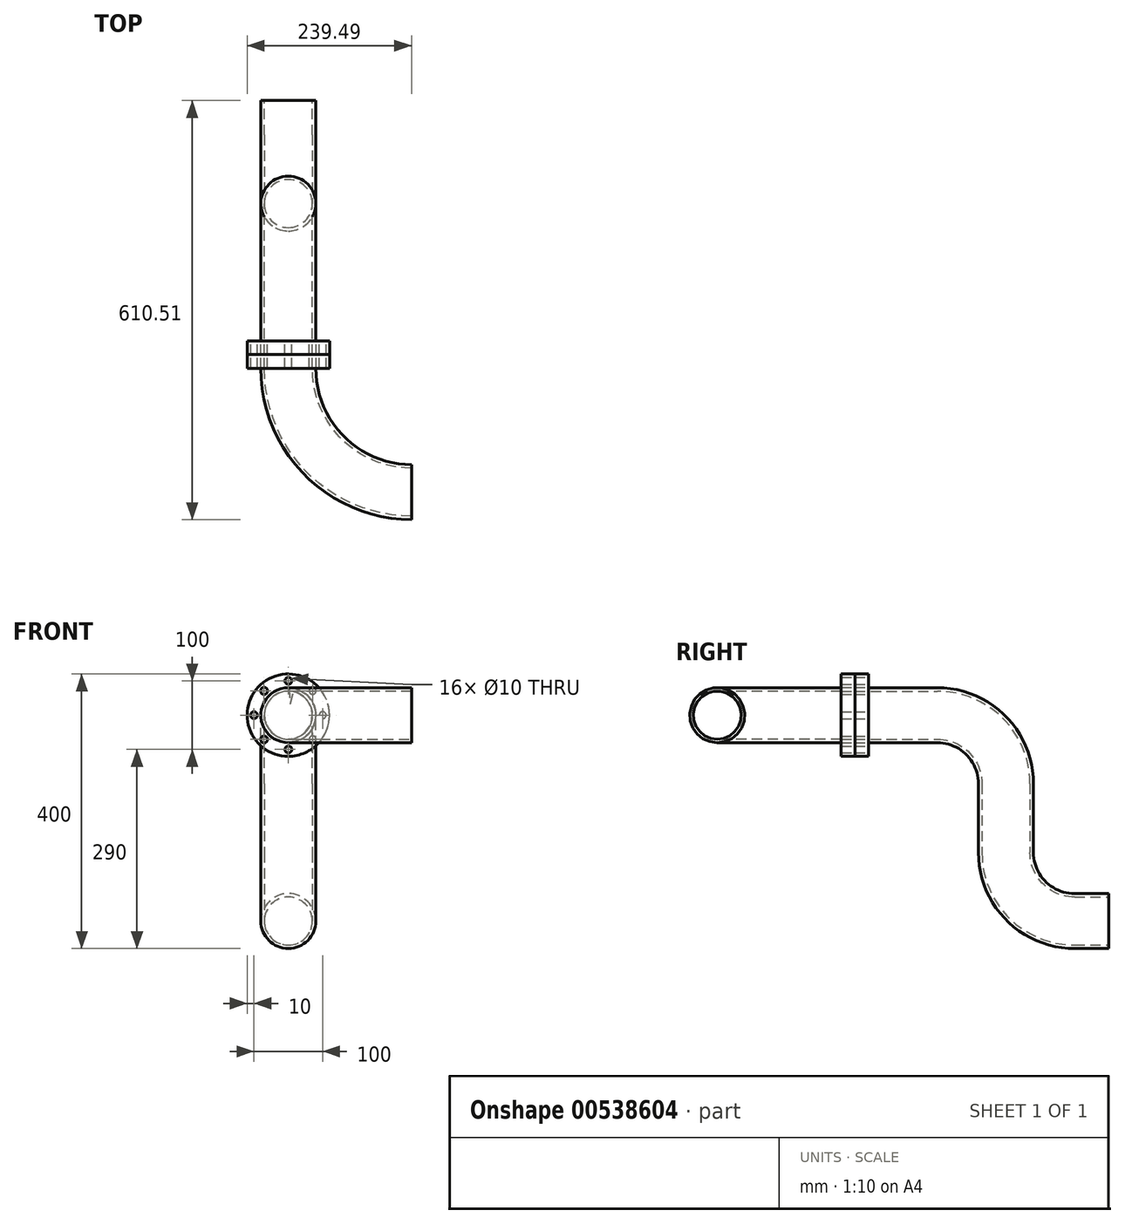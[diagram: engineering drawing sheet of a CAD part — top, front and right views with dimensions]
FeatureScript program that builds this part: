
annotation { "Feature Type Name" : "Feature", "Feature Type Description" : "" }
export const myFeature = defineFeature(function(context is Context, id is Id, definition is map)
    precondition{}
    {
        {
            var Q0;
            Q0=qCreatedBy(makeId("Front.planeOp"),FACE);
            var sketch = newSketch(context, id + "F0", { "sketchPlane" : qUnion([Q0])});
            skCircle(sketch, "E0", {"center": v(0, 0) * mm, "radius": 60 * mm});
            skCircle(sketch, "E1", {"center": v(0, 50) * mm, "radius": 5 * mm});
            skCircle(sketch, "E2.1.0", {"center": v(-35.36, 35.36) * mm, "radius": 5 * mm});
            skCircle(sketch, "E2.2.0", {"center": v(-50, 0) * mm, "radius": 5 * mm});
            skCircle(sketch, "E2.3.0", {"center": v(-35.36, -35.36) * mm, "radius": 5 * mm});
            skCircle(sketch, "E2.4.0", {"center": v(0, -50) * mm, "radius": 5 * mm});
            skCircle(sketch, "E2.5.0", {"center": v(35.36, -35.36) * mm, "radius": 5 * mm});
            skCircle(sketch, "E2.6.0", {"center": v(50, 0) * mm, "radius": 5 * mm});
            skCircle(sketch, "E2.7.0", {"center": v(35.36, 35.36) * mm, "radius": 5 * mm});
            skCircle(sketch, "E3", {"center": v(0, 0) * mm, "radius": 35 * mm});
            skSolve(sketch);
        }
        {
            var Q0;
            Q0 = qSketchRegion(id + "F0", true);
            extrude(context, id + "F1", {"entities" : qUnion([Q0]), "depth" : 20 * mm, "offsetDistance" : 25 * mm});
        }
        {
            var Q0;
            Q0=qCreatedBy(makeId("Front.planeOp"),FACE);
            var sketch = newSketch(context, id + "F2", { "sketchPlane" : qUnion([Q0])});
            skCircle(sketch, "E4", {"center": v(0, 0) * mm, "radius": 40 * mm});
            skCircle(sketch, "E5", {"center": v(0, 0) * mm, "radius": 35 * mm});
            skSolve(sketch);
        }
        {
            var Q0;
            Q0=qCreatedBy(makeId("Right.planeOp"),FACE);
            var sketch = newSketch(context, id + "F3", { "sketchPlane" : qUnion([Q0])});
            skLineSegment(sketch, "E6", {"start": v(0, 0) * mm, "end": v(100, 0) * mm});
            skLineSegment(sketch, "E7", {"start": v(200, -100) * mm, "end": v(200, -200) * mm});
            skLineSegment(sketch, "E8", {"start": v(300, -300) * mm, "end": v(350, -300) * mm});
            skPoint(sketch, "E9.visualSharp", {"position": v(200, 0) * mm});
            skArc(sketch, "E9.filletArc", {"start": v(200, -100) * mm, "mid": v(170.71, -29.29) * mm, "end": v(100, 0) * mm});
            skPoint(sketch, "E10.visualSharp", {"position": v(200, -300) * mm});
            skArc(sketch, "E10.filletArc", {"start": v(200, -200) * mm, "mid": v(229.29, -270.71) * mm, "end": v(300, -300) * mm});
            skSolve(sketch);
        }
        {
            var Q0;
            Q0=makeQuery(id+"F2.imprint","IMPRINT",FACE,{"disambiguationData":[TD([[makeQuery(id+"F2.imprint","IMPRINT",EDGE,{"derivedFrom":sQuery(id+"F2.wireOp",EDGE,"E4")}),1.0]])]});
            var Q1;
            Q1=sQuery(id+"F3.wireOp",EDGE,"E6");
            var Q2;
            Q2=sQuery(id+"F3.wireOp",EDGE,"E9.filletArc");
            var Q3;
            Q3=sQuery(id+"F3.wireOp",EDGE,"E7");
            var Q4;
            Q4=sQuery(id+"F3.wireOp",EDGE,"E10.filletArc");
            var Q5;
            Q5=sQuery(id+"F3.wireOp",EDGE,"E8");
            sweep(context, id + "F4", {"operationType" : NewBodyOperationType.ADD, "profiles" : qUnion([Q0]), "path" : qUnion([Q1, Q2, Q3, Q4, Q5])});
        }
        {
            var Q0;
            Q0=makeQuery(id+"F1.opExtrude","CAP_FACE",FACE,{"disambiguationData":[OSD([sQuery(id+"F0.wireOp",EDGE,"E0"),sQuery(id+"F0.wireOp",EDGE,"E1"),sQuery(id+"F0.wireOp",EDGE,"E2.1.0"),sQuery(id+"F0.wireOp",EDGE,"E2.2.0"),sQuery(id+"F0.wireOp",EDGE,"E2.3.0"),sQuery(id+"F0.wireOp",EDGE,"E2.4.0"),sQuery(id+"F0.wireOp",EDGE,"E2.5.0"),sQuery(id+"F0.wireOp",EDGE,"E2.6.0"),sQuery(id+"F0.wireOp",EDGE,"E2.7.0"),sQuery(id+"F0.wireOp",EDGE,"E3")])],"isStart":false});
            extrude(context, id + "F5", {"entities" : qUnion([Q0]), "depth" : 20 * mm, "offsetDistance" : 25 * mm});
        }
        {
            var Q0;
            Q0=makeQuery(id+"F5.opExtrude","CAP_FACE",FACE,{"disambiguationData":[OSD([sQuery(id+"F0.wireOp",EDGE,"E0"),sQuery(id+"F0.wireOp",EDGE,"E1"),sQuery(id+"F0.wireOp",EDGE,"E2.1.0"),sQuery(id+"F0.wireOp",EDGE,"E2.2.0"),sQuery(id+"F0.wireOp",EDGE,"E2.3.0"),sQuery(id+"F0.wireOp",EDGE,"E2.4.0"),sQuery(id+"F0.wireOp",EDGE,"E2.5.0"),sQuery(id+"F0.wireOp",EDGE,"E2.6.0"),sQuery(id+"F0.wireOp",EDGE,"E2.7.0"),sQuery(id+"F0.wireOp",EDGE,"E3")])],"isStart":false});
            var sketch = newSketch(context, id + "F6", { "sketchPlane" : qUnion([Q0])});
            skCircle(sketch, "E11", {"center": v(0, 0) * mm, "radius": 40 * mm});
            skCircle(sketch, "E12", {"center": v(0, 0) * mm, "radius": 35 * mm});
            skSolve(sketch);
        }
        {
            var Q0;
            Q0=qCreatedBy(makeId("Top.planeOp"),FACE);
            var sketch = newSketch(context, id + "F7", { "sketchPlane" : qUnion([Q0])});
            skLineSegment(sketch, "E13", {"start": v(0, 0) * mm, "end": v(0, -40.5) * mm, "construction": true});
            skLineSegment(sketch, "E14", {"start": v(0, -40.5) * mm, "end": v(180, -40.5) * mm, "construction": true});
            skLineSegment(sketch, "E15", {"start": v(180, -40.5) * mm, "end": v(180, -220.5) * mm, "construction": true});
            skArc(sketch, "E16", {"start": v(180, -220.5) * mm, "mid": v(52.72, -167.79) * mm, "end": v(0, -40.5) * mm});
            skSolve(sketch);
        }
        {
            var Q0;
            Q0=makeQuery(id+"F6.imprint","IMPRINT",FACE,{"disambiguationData":[TD([[makeQuery(id+"F6.imprint","IMPRINT",EDGE,{"derivedFrom":sQuery(id+"F6.wireOp",EDGE,"E11")}),1.0]])]});
            var Q1;
            Q1=sQuery(id+"F7.wireOp",EDGE,"E16");
            sweep(context, id + "F8", {"operationType" : NewBodyOperationType.ADD, "profiles" : qUnion([Q0]), "path" : qUnion([Q1])});
        }
    });
